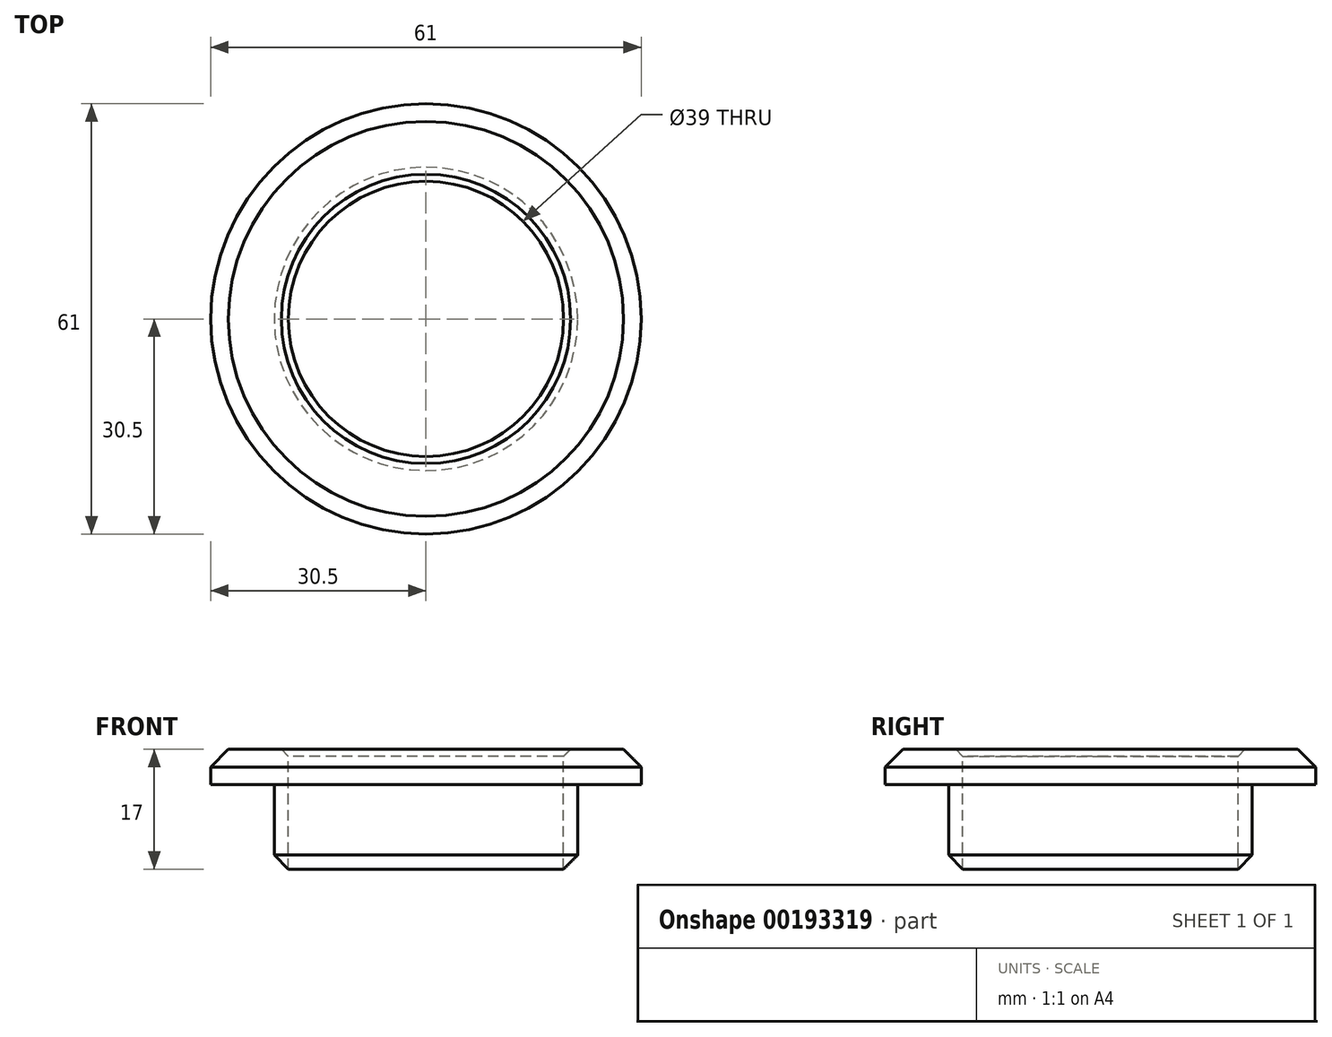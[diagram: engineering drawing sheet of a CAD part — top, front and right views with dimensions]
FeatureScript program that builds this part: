
annotation { "Feature Type Name" : "Feature", "Feature Type Description" : "" }
export const myFeature = defineFeature(function(context is Context, id is Id, definition is map)
    precondition{}
    {
        {
            var Q0;
            Q0=qCreatedBy(makeId("Front.planeOp"),FACE);
            var sketch = newSketch(context, id + "F0", { "sketchPlane" : qUnion([Q0])});
            skLineSegment(sketch, "E0", {"start": v(0, 77.73) * mm, "end": v(0, 0) * mm, "construction": true});
            skLineSegment(sketch, "E1", {"start": v(0, 0) * mm, "end": v(77.73, 0) * mm, "construction": true});
            skLineSegment(sketch, "E2", {"start": v(19.5, -17) * mm, "end": v(19.5, 0) * mm});
            skLineSegment(sketch, "E3", {"start": v(19.5, 0) * mm, "end": v(28, 0) * mm});
            skLineSegment(sketch, "E4", {"start": v(30.5, -2.5) * mm, "end": v(30.5, -5) * mm});
            skLineSegment(sketch, "E5", {"start": v(30.5, -5) * mm, "end": v(21.5, -5) * mm});
            skLineSegment(sketch, "E6", {"start": v(21.5, -5) * mm, "end": v(21.5, -15) * mm});
            skLineSegment(sketch, "E7", {"start": v(21.5, -15) * mm, "end": v(19.5, -17) * mm});
            skLineSegment(sketch, "E8", {"start": v(28, 0) * mm, "end": v(30.5, -2.5) * mm});
            skPoint(sketch, "E9.orphan", {"position": v(30.5, 0) * mm});
            skSolve(sketch);
        }
        {
            var Q0;
            Q0=makeQuery(id+"F0.imprint","IMPRINT",FACE,{"disambiguationData":[TD([[makeQuery(id+"F0.imprint","IMPRINT",EDGE,{"derivedFrom":sQuery(id+"F0.wireOp",EDGE,"E2")}),-1.0]])]});
            var Q1;
            Q1=sQuery(id+"F0.wireOp",EDGE,"E0");
            revolve(context, id + "F1", {"entities" : qUnion([Q0]), "axis" : qUnion([Q1]), "revolveType" : RevolveType.FULL});
        }
        {
            var Q0;
            Q0=makeQuery(id+"F1.opRevolve","SWEPT_EDGE",EDGE,{"disambiguationData":[OSD([sQuery(id+"F0.wireOp",EDGE,"E2"),sQuery(id+"F0.wireOp",EDGE,"E3")])]});
            chamfer(context, id + "F2", {"entities" : qUnion([Q0]), "width" : 1 * mm, "tangentPropagation" : true});
        }
    });
